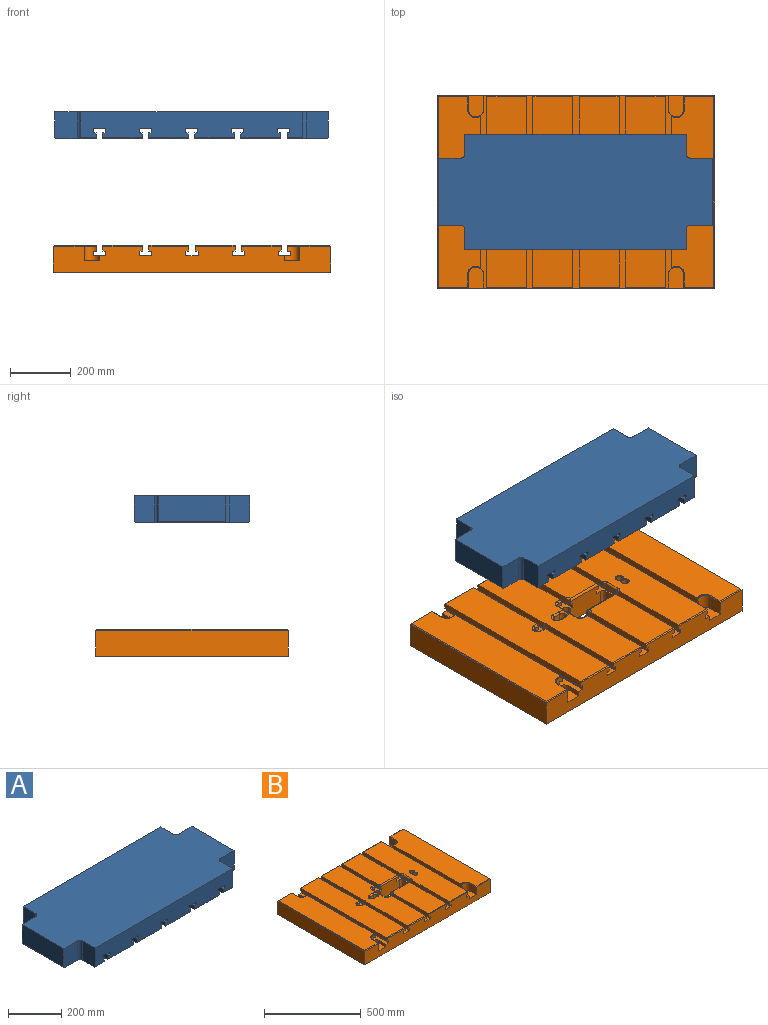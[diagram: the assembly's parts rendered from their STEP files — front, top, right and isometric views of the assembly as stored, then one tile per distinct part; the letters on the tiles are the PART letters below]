
ASSEMBLY  parts=2 mates=1
PART A: 72 faces, bbox 901.7x381x88.9 mm
  f0: plane 222.25x85.73mm, normal (1,0,0), area 19052.4mm2, adj f8,f9,f66,f71
  f1: plane 730.25x85.73mm, normal (0,-1,0), area 57969.9mm2, adj f6,f8,f19,f20,f21,f22,f24,f25
  f2: plane 222.25x85.73mm, normal (-1,0,0), area 19052.4mm2, adj f8,f10,f61,f64
  f3: plane 730.25x85.73mm, normal (0,1,0), area 57969.9mm2, adj f5,f8,f15,f16,f17,f18,f23,f25
  f4: plane 374.65x132.56mm, normal (0,0,-1), area 37150.8mm2, adj f6,f9,f18,f30,f66,f67,f68,f69
  f5: plane 50.01x3.18mm, normal (0,0.71,-0.71), area 224.5mm2, adj f3,f7,f58,f63
  f6: plane 50.01x3.18mm, normal (0,-0.71,-0.71), area 224.5mm2, adj f1,f4,f30,f68
  f7: plane 374.65x132.56mm, normal (0,0,-1), area 37150.8mm2, adj f5,f10,f19,f58,f60,f61,f62,f63
  f8: plane 901.7x381mm, normal (0,0,1), area 316468.5mm2, adj f0,f1,f2,f3,f60,f61,f62,f63
  f9: plane 222.25x3.18mm, normal (0.71,0,-0.71), area 997.9mm2, adj f0,f4,f66,f71
  f10: plane 222.25x3.18mm, normal (-0.71,0,-0.71), area 997.9mm2, adj f2,f7,f61,f64
  f11: plane 374.65x131.76mm, normal (0,0,-1), area 49364.8mm2, adj f23,f24,f52,f59
  f12: plane 374.65x131.76mm, normal (0,0,-1), area 49364.8mm2, adj f15,f20,f38,f51
  f13: plane 374.65x131.76mm, normal (0,0,-1), area 49364.8mm2, adj f16,f21,f31,f44
  f14: plane 374.65x131.76mm, normal (0,0,-1), area 49364.8mm2, adj f17,f22,f37,f45
  f15: plane 131.76x3.18mm, normal (0,0.71,-0.71), area 591.6mm2, adj f3,f12,f38,f51
  f16: plane 131.76x3.18mm, normal (0,0.71,-0.71), area 591.6mm2, adj f3,f13,f31,f44
  f17: plane 131.76x3.18mm, normal (0,0.71,-0.71), area 591.6mm2, adj f3,f14,f37,f45
  f18: plane 50.01x3.18mm, normal (0,0.71,-0.71), area 224.5mm2, adj f3,f4,f30,f69
  f19: plane 50.01x3.18mm, normal (0,-0.71,-0.71), area 224.5mm2, adj f1,f7,f58,f62
  f20: plane 131.76x3.18mm, normal (0,-0.71,-0.71), area 591.6mm2, adj f1,f12,f38,f51
  f21: plane 131.76x3.18mm, normal (0,-0.71,-0.71), area 591.6mm2, adj f1,f13,f31,f44
  f22: plane 131.76x3.18mm, normal (0,-0.71,-0.71), area 591.6mm2, adj f1,f14,f37,f45
  f23: plane 131.76x3.18mm, normal (0,0.71,-0.71), area 591.6mm2, adj f3,f11,f52,f59
  f24: plane 131.76x3.18mm, normal (0,-0.71,-0.71), area 591.6mm2, adj f1,f11,f52,f59
  f25: plane 381x9.53mm, normal (0,0,1), area 3629mm2, adj f1,f3,f29,f30
  f26: plane 381x9.53mm, normal (0,0,1), area 3629mm2, adj f1,f3,f27,f31
  f27: plane 381x15.08mm, normal (1,0,0), area 5746mm2, adj f1,f3,f26,f28
  f28: plane 381x39.69mm, normal (0,0,-1), area 15120.9mm2, adj f1,f3,f27,f29
  f29: plane 381x15.08mm, normal (-1,0,0), area 5746mm2, adj f1,f3,f25,f28
  f30: plane 381x19.05mm, normal (-1,0,0), area 7248mm2, adj f1,f3,f4,f6,f18,f25
  f31: plane 381x19.05mm, normal (1,0,0), area 7248mm2, adj f1,f3,f13,f16,f21,f26
  f32: plane 381x9.53mm, normal (0,0,1), area 3629mm2, adj f1,f3,f36,f37
  f33: plane 381x9.53mm, normal (0,0,1), area 3629mm2, adj f1,f3,f34,f38
  f34: plane 381x15.08mm, normal (1,0,0), area 5746mm2, adj f1,f3,f33,f35
  f35: plane 381x39.69mm, normal (0,0,-1), area 15120.9mm2, adj f1,f3,f34,f36
  f36: plane 381x15.08mm, normal (-1,0,0), area 5746mm2, adj f1,f3,f32,f35
  f37: plane 381x19.05mm, normal (-1,0,0), area 7248mm2, adj f1,f3,f14,f17,f22,f32
  f38: plane 381x19.05mm, normal (1,0,0), area 7248mm2, adj f1,f3,f12,f15,f20,f33
  f39: plane 381x9.53mm, normal (0,0,1), area 3629mm2, adj f1,f3,f40,f45
  f40: plane 381x15.08mm, normal (1,0,0), area 5746mm2, adj f1,f3,f39,f41
  f41: plane 381x39.69mm, normal (0,0,-1), area 15120.9mm2, adj f1,f3,f40,f42
  f42: plane 381x15.08mm, normal (-1,0,0), area 5746mm2, adj f1,f3,f41,f43
  f43: plane 381x9.53mm, normal (0,0,1), area 3629mm2, adj f1,f3,f42,f44
  f44: plane 381x19.05mm, normal (-1,0,0), area 7248mm2, adj f1,f3,f13,f16,f21,f43
  f45: plane 381x19.05mm, normal (1,0,0), area 7248mm2, adj f1,f3,f14,f17,f22,f39
  f46: plane 381x9.53mm, normal (0,0,1), area 3629mm2, adj f1,f3,f50,f51
  f47: plane 381x9.53mm, normal (0,0,1), area 3629mm2, adj f1,f3,f48,f52
  f48: plane 381x15.08mm, normal (1,0,0), area 5746mm2, adj f1,f3,f47,f49
  f49: plane 381x39.69mm, normal (0,0,-1), area 15120.9mm2, adj f1,f3,f48,f50
  f50: plane 381x15.08mm, normal (-1,0,0), area 5746mm2, adj f1,f3,f46,f49
  f51: plane 381x19.05mm, normal (-1,0,0), area 7248mm2, adj f1,f3,f12,f15,f20,f46
  f52: plane 381x19.05mm, normal (1,0,0), area 7248mm2, adj f1,f3,f11,f23,f24,f47
  f53: plane 381x9.53mm, normal (0,0,1), area 3629mm2, adj f1,f3,f54,f58
  f54: plane 381x15.08mm, normal (1,0,0), area 5746mm2, adj f1,f3,f53,f55
  f55: plane 381x39.69mm, normal (0,0,-1), area 15120.9mm2, adj f1,f3,f54,f56
  f56: plane 381x15.08mm, normal (-1,0,0), area 5746mm2, adj f1,f3,f55,f57
  f57: plane 381x9.53mm, normal (0,0,1), area 3629mm2, adj f1,f3,f56,f59
  f58: plane 381x19.05mm, normal (1,0,0), area 7248mm2, adj f1,f3,f5,f7,f19,f53
  f59: plane 381x19.05mm, normal (-1,0,0), area 7248mm2, adj f1,f3,f11,f23,f24,f57
  f60: cylinder r=12.7mm len=88.9mm, axis (0,0,1), area 1773.5mm2, adj f7,f8,f61,f62
  f61: plane 88.9x73.03mm, normal (0,-1,0), area 6486.9mm2, adj f2,f7,f8,f10,f60
  f62: plane 88.9x66.68mm, normal (-1,0,0), area 5922.4mm2, adj f1,f7,f8,f19,f60
  f63: plane 88.9x66.68mm, normal (-1,0,0), area 5922.4mm2, adj f3,f5,f7,f8,f65
  f64: plane 88.9x73.03mm, normal (0,1,0), area 6486.9mm2, adj f2,f7,f8,f10,f65
  f65: cylinder r=12.7mm len=88.9mm, axis (0,0,1), area 1773.5mm2, adj f7,f8,f63,f64
  f66: plane 88.9x73.03mm, normal (0,-1,0), area 6486.9mm2, adj f0,f4,f8,f9,f67
  f67: cylinder r=12.7mm len=88.9mm, axis (0,0,1), area 1773.5mm2, adj f4,f8,f66,f68
  f68: plane 88.9x66.68mm, normal (1,0,0), area 5922.4mm2, adj f1,f4,f6,f8,f67
  f69: plane 88.9x66.68mm, normal (1,0,0), area 5922.4mm2, adj f3,f4,f8,f18,f70
  f70: cylinder r=12.7mm len=88.9mm, axis (0,0,1), area 1773.5mm2, adj f4,f8,f69,f71
  f71: plane 88.9x73.03mm, normal (0,1,0), area 6486.9mm2, adj f0,f4,f8,f9,f70
PART B: 155 faces, bbox 914.4x635x88.9 mm
  f0: plane 628.65x131.76mm, normal (0,0,1), area 81687.9mm2, adj f20,f47,f48,f72,f75,f136,f137,f138
  f1: plane 628.65x131.76mm, normal (0,0,1), area 81050.8mm2, adj f14,f36,f41,f53,f65,f129,f130,f131
  f2: plane 269.88x131.76mm, normal (0,0,1), area 35460.9mm2, adj f15,f37,f59,f139,f140
  f3: plane 914.4x635mm, normal (0,0,-1), area 560343.8mm2, adj f24,f43,f44,f45,f92,f93,f94,f95
  f4: plane 279.4x9.53mm, normal (0,0,-1), area 2634.2mm2, adj f8,f24,f59,f97,f102,f111
  f5: plane 260.35x9.53mm, normal (0,0,-1), area 2479.8mm2, adj f6,f10,f24,f106
  f6: plane 260.35x15.08mm, normal (1,0,0), area 3926.4mm2, adj f5,f7,f24,f106
  f7: plane 279.4x39.69mm, normal (0,0,1), area 10503.3mm2, adj f6,f8,f24,f102,f105,f106,f107
  f8: plane 279.4x15.08mm, normal (-1,0,0), area 4213.7mm2, adj f4,f7,f24,f102
  f9: plane 265.65x19.05mm, normal (-1,0,0), area 5042.5mm2, adj f34,f42,f44,f54,f109,f142
  f10: plane 260.35x19.05mm, normal (1,0,0), area 4946mm2, adj f5,f24,f33,f35,f106,f124
  f11: plane 279.4x9.53mm, normal (0,0,-1), area 2661.3mm2, adj f12,f15,f24,f102
  f12: plane 279.4x15.08mm, normal (1,0,0), area 4213.7mm2, adj f11,f13,f24,f102
  f13: plane 635x39.69mm, normal (0,0,1), area 22791mm2, adj f12,f24,f44,f62,f63,f99,f100,f101
  f14: plane 284.7x19.05mm, normal (-1,0,0), area 5405.4mm2, adj f1,f24,f36,f64,f116,f131
  f15: plane 279.4x19.05mm, normal (1,0,0), area 5308.9mm2, adj f2,f11,f24,f37,f102,f139
  f16: plane 304.8x9.53mm, normal (0,0,-1), area 2903.2mm2, adj f17,f20,f24,f93
  f17: plane 304.8x15.08mm, normal (1,0,0), area 4596.8mm2, adj f16,f18,f24,f93
  f18: plane 635x39.69mm, normal (0,0,1), area 24444.2mm2, adj f17,f24,f44,f69,f70,f92,f93,f94
  f19: plane 310.1x19.05mm, normal (-1,0,0), area 5902.3mm2, adj f33,f40,f44,f67,f96
  f20: plane 304.8x19.05mm, normal (1,0,0), area 5792.7mm2, adj f0,f16,f24,f47,f93,f136
  f21: plane 628.65x138.91mm, normal (0,0,1), area 81781.9mm2, adj f23,f28,f38,f46,f147,f148,f153,f154
  f22: plane 101.6x3.18mm, normal (0,-0.71,0.71), area 447.4mm2, adj f24,f25,f49,f78,f152
  f23: plane 101.6x3.18mm, normal (0,0.71,0.71), area 447.4mm2, adj f21,f44,f46,f90,f148
  f24: plane 914.4x85.73mm, normal (0,-1,0), area 69843.6mm2, adj f3,f4,f5,f6,f7,f8,f10,f11
  f25: plane 628.65x138.91mm, normal (0,0,1), area 81781.9mm2, adj f22,f32,f39,f49,f149,f150,f151,f152
  f26: plane 505.22x9.53mm, normal (0,0,-1), area 4763.2mm2, adj f27,f28,f85,f89
  f27: plane 496.53x15.08mm, normal (-1,0,0), area 7488.3mm2, adj f26,f52,f85,f89
  f28: plane 505.22x19.05mm, normal (-1,0,0), area 9621.5mm2, adj f21,f26,f85,f89,f147,f153
  f29: plane 505.22x9.53mm, normal (0,0,-1), area 4763.2mm2, adj f30,f32,f77,f81
  f30: plane 496.53x15.08mm, normal (1,0,0), area 7488.3mm2, adj f29,f31,f77,f81
  f31: plane 635x39.69mm, normal (0,0,1), area 22704mm2, adj f24,f30,f44,f73,f76,f77,f80,f81
  f32: plane 505.22x19.05mm, normal (1,0,0), area 9621.5mm2, adj f25,f29,f77,f81,f149,f151
  f33: plane 628.65x131.76mm, normal (0,0,1), area 76521.8mm2, adj f10,f19,f35,f40,f60,f71,f96,f124
  f34: plane 269.88x131.76mm, normal (0,0,1), area 35460.9mm2, adj f9,f42,f66,f142,f143
  f35: plane 131.76x3.18mm, normal (0,-0.71,0.71), area 591.6mm2, adj f10,f24,f33,f71
  f36: plane 131.76x3.18mm, normal (0,-0.71,0.71), area 591.6mm2, adj f1,f14,f24,f53
  f37: plane 131.76x3.18mm, normal (0,-0.71,0.71), area 591.6mm2, adj f2,f15,f24,f59
  f38: plane 101.6x3.18mm, normal (0,-0.71,0.71), area 447.4mm2, adj f21,f24,f46,f86,f154
  f39: plane 101.6x3.18mm, normal (0,0.71,0.71), area 447.4mm2, adj f25,f44,f49,f82,f150
  f40: plane 131.76x3.18mm, normal (0,0.71,0.71), area 591.6mm2, adj f19,f33,f44,f60
  f41: plane 131.76x3.18mm, normal (0,0.71,0.71), area 591.6mm2, adj f1,f44,f53,f65
  f42: plane 131.76x3.18mm, normal (0,0.71,0.71), area 591.6mm2, adj f9,f34,f44,f66
  f43: plane 635x85.73mm, normal (1,0,0), area 54435.4mm2, adj f3,f24,f44,f46
  f44: plane 914.4x85.73mm, normal (0,1,0), area 69843.6mm2, adj f3,f9,f13,f18,f19,f23,f31,f39
  f45: plane 635x85.73mm, normal (-1,0,0), area 54435.4mm2, adj f3,f24,f44,f49
  f46: plane 635x3.18mm, normal (0.71,0,0.71), area 2837mm2, adj f21,f23,f38,f43
  f47: plane 131.76x3.18mm, normal (0,-0.71,0.71), area 591.6mm2, adj f0,f20,f24,f75
  f48: plane 131.76x3.18mm, normal (0,0.71,0.71), area 591.6mm2, adj f0,f44,f72,f75
  f49: plane 635x3.18mm, normal (-0.71,0,0.71), area 2837mm2, adj f22,f25,f39,f45
  f50: plane 635x9.53mm, normal (0,0,-1), area 6048.4mm2, adj f24,f44,f51,f53
  f51: plane 635x15.08mm, normal (1,0,0), area 9576.6mm2, adj f24,f44,f50,f52
  f52: plane 635x39.69mm, normal (0,0,1), area 22704mm2, adj f24,f27,f44,f51,f84,f85,f88,f89
  f53: plane 635x19.05mm, normal (1,0,0), area 12086.7mm2, adj f1,f24,f36,f41,f44,f50
  f54: plane 279.4x9.53mm, normal (0,0,-1), area 2634.2mm2, adj f9,f44,f58,f99,f109,f110
  f55: plane 260.35x9.53mm, normal (0,0,-1), area 2479.8mm2, adj f44,f56,f60,f98
  f56: plane 260.35x15.08mm, normal (1,0,0), area 3926.4mm2, adj f44,f55,f57,f98
  f57: plane 279.4x39.69mm, normal (0,0,1), area 10503.3mm2, adj f44,f56,f58,f98,f99,f104,f108
  f58: plane 279.4x15.08mm, normal (-1,0,0), area 4213.7mm2, adj f44,f54,f57,f99
  f59: plane 265.65x19.05mm, normal (-1,0,0), area 5042.5mm2, adj f2,f4,f24,f37,f97,f140
  f60: plane 260.35x19.05mm, normal (1,0,0), area 4946mm2, adj f33,f40,f44,f55,f98,f128
  f61: plane 279.4x9.53mm, normal (0,0,-1), area 2661.3mm2, adj f44,f62,f66,f99
  f62: plane 279.4x15.08mm, normal (1,0,0), area 4213.7mm2, adj f13,f44,f61,f99
  f63: plane 635x15.08mm, normal (-1,0,0), area 9576.6mm2, adj f13,f24,f44,f64
  f64: plane 635x9.53mm, normal (0,0,-1), area 5903.4mm2, adj f14,f24,f44,f63,f65,f115,f116,f117
  f65: plane 284.7x19.05mm, normal (-1,0,0), area 5405.4mm2, adj f1,f41,f44,f64,f117,f129
  f66: plane 279.4x19.05mm, normal (1,0,0), area 5308.9mm2, adj f34,f42,f44,f61,f99,f143
  f67: plane 635x9.53mm, normal (0,0,-1), area 6024.4mm2, adj f19,f24,f44,f70,f71,f96
  f68: plane 304.8x9.53mm, normal (0,0,-1), area 2903.2mm2, adj f44,f69,f72,f92
  f69: plane 304.8x15.08mm, normal (1,0,0), area 4596.8mm2, adj f18,f44,f68,f92
  f70: plane 635x15.08mm, normal (-1,0,0), area 9576.6mm2, adj f18,f24,f44,f67
  f71: plane 310.1x19.05mm, normal (-1,0,0), area 5902.3mm2, adj f24,f33,f35,f67,f96
  f72: plane 304.8x19.05mm, normal (1,0,0), area 5792.7mm2, adj f0,f44,f48,f68,f92,f138
  f73: plane 635x15.08mm, normal (-1,0,0), area 9576.6mm2, adj f24,f31,f44,f74
  f74: plane 635x9.53mm, normal (0,0,-1), area 6048.4mm2, adj f24,f44,f73,f75
  f75: plane 635x19.05mm, normal (-1,0,0), area 12086.7mm2, adj f0,f24,f44,f47,f48,f74
  f76: plane 44.45x16.67mm, normal (-1,0,0), area 740.9mm2, adj f24,f31,f77,f79
  f77: cylinder r=25.4mm len=50.8mm, axis (0,0,1), area 2951.6mm2, adj f29,f30,f31,f32,f76,f78,f79,f151
  f78: plane 48.44x44.45mm, normal (1,0,0), area 2152.7mm2, adj f22,f24,f77,f79,f152
  f79: plane 69.85x50.8mm, normal (0,0,1), area 3271.5mm2, adj f24,f76,f77,f78
  f80: plane 44.45x16.67mm, normal (-1,0,0), area 740.9mm2, adj f31,f44,f81,f83
  f81: cylinder r=25.4mm len=50.8mm, axis (0,0,1), area 2951.6mm2, adj f29,f30,f31,f32,f80,f82,f83,f149
  f82: plane 48.44x44.45mm, normal (1,0,0), area 2152.7mm2, adj f39,f44,f81,f83,f150
  f83: plane 69.85x50.8mm, normal (0,0,1), area 3271.5mm2, adj f44,f80,f81,f82
  f84: plane 44.45x16.67mm, normal (1,0,0), area 740.9mm2, adj f24,f52,f85,f87
  f85: cylinder r=25.4mm len=50.8mm, axis (0,0,1), area 2951.6mm2, adj f26,f27,f28,f52,f84,f86,f87,f153
  f86: plane 48.44x44.45mm, normal (-1,0,0), area 2152.7mm2, adj f24,f38,f85,f87,f154
  f87: plane 69.85x50.8mm, normal (0,0,1), area 3271.5mm2, adj f24,f84,f85,f86
  f88: plane 44.45x16.67mm, normal (1,0,0), area 740.9mm2, adj f44,f52,f89,f91
  f89: cylinder r=25.4mm len=50.8mm, axis (0,0,1), area 2951.6mm2, adj f26,f27,f28,f52,f88,f90,f91,f147
  f90: plane 48.44x44.45mm, normal (-1,0,0), area 2152.7mm2, adj f23,f44,f89,f91,f148
  f91: plane 69.85x50.8mm, normal (0,0,1), area 3271.5mm2, adj f44,f88,f89,f90
  f92: plane 82.55x25.4mm, normal (0,-1,0), area 1666.5mm2, adj f3,f18,f68,f69,f72,f94,f95,f138
  f93: plane 82.55x25.4mm, normal (0,1,0), area 1666.5mm2, adj f3,f16,f17,f18,f20,f94,f95,f136
  f94: cylinder r=12.7mm len=54.77mm, axis (0,0,1), area 2185.2mm2, adj f3,f18,f92,f93
  f95: cylinder r=12.7mm len=82.55mm, axis (0,0,1), area 3293.6mm2, adj f3,f92,f93,f137
  f96: cylinder r=12.7mm len=19.05mm, axis (0,0,1), area 301.1mm2, adj f19,f33,f67,f71
  f97: cylinder r=12.7mm len=12.7mm, axis (0,0,1), area 100.4mm2, adj f4,f59,f111,f140
  f98: plane 82.55x25.4mm, normal (0,-1,0), area 1666.5mm2, adj f3,f55,f56,f57,f60,f108,f114,f128
  f99: plane 139.7x82.55mm, normal (0,-1,0), area 10994.2mm2, adj f3,f13,f54,f57,f58,f61,f62,f66
  f100: cylinder r=12.7mm len=54.77mm, axis (0,0,1), area 1092.6mm2, adj f3,f13,f99,f101
  f101: plane 54.77x50.8mm, normal (-1,0,0), area 2782.3mm2, adj f3,f13,f100,f103
  f102: plane 139.7x82.55mm, normal (0,1,0), area 10994.2mm2, adj f3,f4,f7,f8,f11,f12,f13,f15
  f103: cylinder r=12.7mm len=54.77mm, axis (0,0,1), area 1092.6mm2, adj f3,f13,f101,f102
  f104: plane 54.77x6.35mm, normal (-1,0,0), area 347.8mm2, adj f3,f57,f99,f108
  f105: plane 54.77x6.35mm, normal (-1,0,0), area 347.8mm2, adj f3,f7,f102,f107
  f106: plane 82.55x25.4mm, normal (0,1,0), area 1666.5mm2, adj f3,f5,f6,f7,f10,f107,f112,f124
  f107: cylinder r=12.7mm len=54.77mm, axis (0,0,1), area 1092.6mm2, adj f3,f7,f105,f106
  f108: cylinder r=12.7mm len=54.77mm, axis (0,0,1), area 1092.6mm2, adj f3,f57,f98,f104
  f109: cylinder r=12.7mm len=12.7mm, axis (0,0,1), area 100.4mm2, adj f9,f54,f110,f142
  f110: plane 12.7x6.35mm, normal (-1,0,0), area 80.6mm2, adj f54,f99,f109,f144
  f111: plane 12.7x6.35mm, normal (-1,0,0), area 80.6mm2, adj f4,f97,f102,f141
  f112: cylinder r=12.7mm len=82.55mm, axis (0,0,1), area 1646.8mm2, adj f3,f106,f113,f125
  f113: plane 88.9x82.55mm, normal (1,0,0), area 7338.7mm2, adj f3,f112,f114,f126
  f114: cylinder r=12.7mm len=82.55mm, axis (0,0,1), area 1646.8mm2, adj f3,f98,f113,f127
  f115: plane 50.8x12.7mm, normal (-1,0,0), area 645.2mm2, adj f64,f116,f117,f130
  f116: cylinder r=12.7mm len=12.7mm, axis (0,0,1), area 100.4mm2, adj f14,f64,f115,f131
  f117: cylinder r=12.7mm len=12.7mm, axis (0,0,1), area 100.4mm2, adj f64,f65,f115,f129
  f118: cylinder r=11.18mm len=86.54mm, axis (0,0,1), area 6076.8mm2, adj f3,f145
  f119: cylinder r=12.7mm len=82.55mm, axis (0,0,1), area 3293.6mm2, adj f3,f120,f122,f133
  f120: plane 82.55x25.4mm, normal (0,-1,0), area 2096.8mm2, adj f3,f119,f121,f135
  f121: cylinder r=12.7mm len=82.55mm, axis (0,0,1), area 3293.6mm2, adj f3,f120,f122,f134
  f122: plane 82.55x25.4mm, normal (0,1,0), area 2096.8mm2, adj f3,f119,f121,f132
  f123: cylinder r=11.18mm len=86.54mm, axis (0,0,1), area 6076.8mm2, adj f3,f146
  f124: cylinder r=6.35mm len=15.08mm, axis (-1,0,0), area 150.4mm2, adj f10,f33,f106,f125
  f125: torus R=19.05mm, axis (0,0,1), area 235.1mm2, adj f33,f112,f124,f126
  f126: cylinder r=6.35mm len=88.9mm, axis (0,1,0), area 886.7mm2, adj f33,f113,f125,f127
  f127: torus R=19.05mm, axis (0,0,1), area 235.1mm2, adj f33,f114,f126,f128
  f128: cylinder r=6.35mm len=15.08mm, axis (1,0,0), area 150.4mm2, adj f33,f60,f98,f127
  f129: torus R=19.05mm, axis (0,0,1), area 120.6mm2, adj f1,f65,f117,f130
  f130: cylinder r=6.35mm len=50.8mm, axis (0,-1,0), area 506.7mm2, adj f1,f115,f129,f131
  f131: torus R=19.05mm, axis (0,0,1), area 120.6mm2, adj f1,f14,f116,f130
  f132: cylinder r=6.35mm len=25.4mm, axis (-1,0,0), area 253.4mm2, adj f33,f122,f133,f134
  f133: torus R=19.05mm, axis (0,0,1), area 470.3mm2, adj f33,f119,f132,f135
  f134: torus R=19.05mm, axis (0,0,1), area 470.3mm2, adj f33,f121,f132,f135
  f135: cylinder r=6.35mm len=25.4mm, axis (1,0,0), area 253.4mm2, adj f33,f120,f133,f134
  f136: cylinder r=6.35mm len=15.08mm, axis (-1,0,0), area 150.4mm2, adj f0,f20,f93,f137
  f137: torus R=19.05mm, axis (0,0,1), area 470.3mm2, adj f0,f95,f136,f138
  f138: cylinder r=6.35mm len=15.08mm, axis (1,0,0), area 150.4mm2, adj f0,f72,f92,f137
  f139: cylinder r=6.35mm len=129.38mm, axis (-1,0,0), area 1267.5mm2, adj f2,f15,f102,f141
  f140: torus R=19.05mm, axis (0,0,1), area 120.6mm2, adj f2,f59,f97,f141
  f141: cylinder r=6.35mm len=6.35mm, axis (0,-1,0), area 40.3mm2, adj f111,f139,f140
  f142: torus R=19.05mm, axis (0,0,1), area 120.6mm2, adj f9,f34,f109,f144
  f143: cylinder r=6.35mm len=129.38mm, axis (1,0,0), area 1267.5mm2, adj f34,f66,f99,f144
  f144: cylinder r=6.35mm len=6.35mm, axis (0,-1,0), area 40.3mm2, adj f110,f142,f143
  f145: torus R=13.54mm, axis (0,0,1), area 275.2mm2, adj f1,f118,f146
  f146: torus R=13.54mm, axis (0,0,1), area 275.2mm2, adj f1,f123,f145
  f147: torus R=27.76mm, axis (0,0,1), area 212.7mm2, adj f21,f28,f89,f148
  f148: cylinder r=2.36mm len=43.64mm, axis (0,-1,0), area 156.3mm2, adj f21,f23,f90,f147
  f149: torus R=27.76mm, axis (0,0,1), area 212.7mm2, adj f25,f32,f81,f150
  f150: cylinder r=2.36mm len=43.64mm, axis (0,1,0), area 156.3mm2, adj f25,f39,f82,f149
  f151: torus R=27.76mm, axis (0,0,1), area 212.7mm2, adj f25,f32,f77,f152
  f152: cylinder r=2.36mm len=43.64mm, axis (0,1,0), area 156.3mm2, adj f22,f25,f78,f151
  f153: torus R=27.76mm, axis (0,0,1), area 212.7mm2, adj f21,f28,f85,f154
  f154: cylinder r=2.36mm len=43.64mm, axis (0,-1,0), area 156.3mm2, adj f21,f38,f86,f153
PLACE A t=(-5.19,69.08,530.09)mm
PLACE B t=(-3.69,69.08,0)mm
MATE slider A.f12 <-> B.f33  axis (0,0,-1) through (-5.19,69.08,441.19)mm
